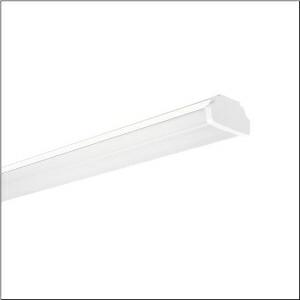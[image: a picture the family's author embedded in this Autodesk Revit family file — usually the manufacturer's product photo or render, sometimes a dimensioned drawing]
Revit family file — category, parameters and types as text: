
# Revit family: modario_r__31_ho_53bm811d2v4120_c329
name_source: partatom
category: Lighting Fixtures
units: mm (PartAtom-declared; Revit-internal decimal feet)

## family parameters
Cut with Voids When Loaded = No
Host = Face
Light Source = No
Part Type = Normal
Room Calculation Point = No
Round Connector Dimension = Use Diameter
Shared = No

## types (1)
- --- (1 x LED, 12350 lm, 79.5 W, 4000K)
    Apparent Load = 80 VA
    CIE Flux Codes = 52 78 94 90 100
    Color Rendering = 80
    Color Temperature = 4000K
    Default Elevation = 1800 mm
    Description = Modario® 31 HO, luminaire insert, of sheet steel, coil coated, white, length: 1.495mm, width: 81mm, height: 82mm, LED rated luminous flux: 12.350lm, light colour: 840, control gear: DALI 2, control gear: ECG DALI, with plug, 5-pole, with phase selection, mains connection: 220..240V, AC, 50/60Hz, primary optical cover: cover, of PMMA, light emission: direct distribution, primary light characteristic: symmetric, protection rating (complete): IP20, protection rating (LED compartment): IP50, insulation class (complete): insulation class I (protective earthing), certification: CE, ENEC, VDE, UKCA, permissible ambient temperature for indoor applications: -25..+30°C, corresponds to IFS (International Featured Standards) requirements for safety and quality in the food industry, reducing of maximum allowable ambient temperature of 5°C with ceiling mounting, packaging unit: 1 piece
    Height = 92 mm
    Lamp = 1 x LED
    Lamp Light Flux = 12350 lm
    Lamp Power = 79.5 W
    Lamp count = 1
    Length = 1495 mm
    Luminous efficacy = 155 lm/W
    Manufacturer = Siteco
    ModVariant = No
    Model = 53BM811D2V4120
    Mounting Place = Ceiling
    Mounting Type = Pendant
    Number of Poles = 1
    OnlyDefault = Yes
    Power Factor = 1
    Product Name = Modario® 31 HO
    Product group = luminaire insert
    ProductGroupID = 902
    Protection Class = Protection class I
    Protection Degree = IP 20
    RLX_Detail_Level = 1
    RlxData = <blob elided: 42181 chars, md5=4e766544>
    Socket = socket
    Standby Power = 0 W
    System Light Flux = 12350 lm
    System Power = 80 W
    Type Comments = factory setting: luminous flux: 100 % | dim-lin: 254 | 345 mA
    Type Image = l_1003447.jpg
    URL = http://relux.com
    VarID = @adj_126431
    Voltage = 0 V
    Weight = 0.00 kg
    Width = 81 mm

## geometry (parser evidence)
native form markers: Blend x4, Sweep x11
no freeform markers — native parametric forms only
